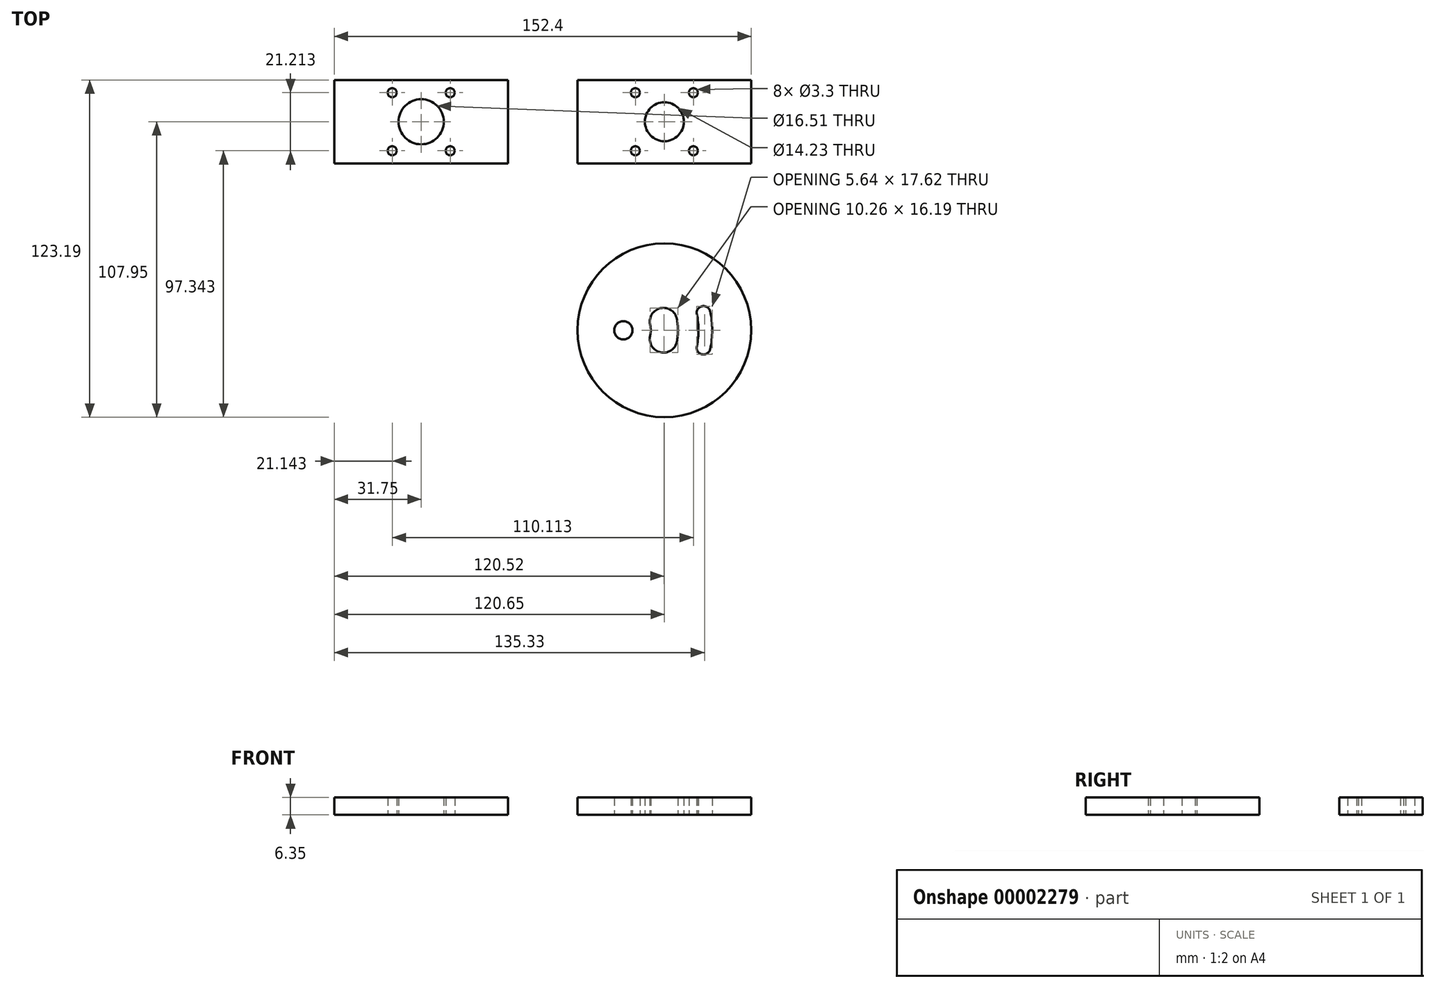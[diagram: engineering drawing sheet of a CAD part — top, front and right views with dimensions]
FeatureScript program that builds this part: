
annotation { "Feature Type Name" : "Feature", "Feature Type Description" : "" }
export const myFeature = defineFeature(function(context is Context, id is Id, definition is map)
    precondition{}
    {
        {
            var Q0;
            Q0=qCreatedBy(makeId("Top.planeOp"),FACE);
            var sketch = newSketch(context, id + "F0", { "sketchPlane" : qUnion([Q0])});
            skCircle(sketch, "E0", {"center": v(0, 0) * mm, "radius": 8.26 * mm});
            skCircle(sketch, "E1", {"center": v(88.9, 0) * mm, "radius": 7.12 * mm});
            skCircle(sketch, "E2", {"center": v(88.9, -76.2) * mm, "radius": 31.75 * mm});
            skCircle(sketch, "E3", {"center": v(73.9, -76.2) * mm, "radius": 3.35 * mm});
            skCircle(sketch, "E4", {"center": v(73.9, -76.2) * mm, "radius": 30 * mm, "construction": true});
            skArc(sketch, "E5", {"start": v(100.78, -82.02) * mm, "mid": v(101.4, -76.2) * mm, "end": v(100.78, -70.38) * mm});
            skArc(sketch, "E6", {"start": v(105.66, -83.08) * mm, "mid": v(106.4, -76.2) * mm, "end": v(105.66, -69.32) * mm});
            skCircle(sketch, "E7", {"center": v(88.9, -76.2) * mm, "radius": 15 * mm, "construction": true});
            skArc(sketch, "E8", {"start": v(103.4, -72.34) * mm, "mid": v(103.52, -72.33) * mm, "end": v(103.65, -72.31) * mm});
            skArc(sketch, "E9", {"start": v(100.78, -82.02) * mm, "mid": v(102.7, -85) * mm, "end": v(105.66, -83.08) * mm});
            skArc(sketch, "E10.trimOffspring", {"start": v(105.66, -69.32) * mm, "mid": v(102.7, -67.4) * mm, "end": v(100.78, -70.38) * mm});
            skArc(sketch, "E11.trimOffspring", {"start": v(103.65, -80.09) * mm, "mid": v(103.52, -80.07) * mm, "end": v(103.4, -80.06) * mm});
            skCircle(sketch, "E12", {"center": v(73.9, -76.2) * mm, "radius": 15 * mm, "construction": true});
            skArc(sketch, "E13", {"start": v(93.45, -71.97) * mm, "mid": v(87.5, -68.14) * mm, "end": v(83.67, -74.08) * mm});
            skArc(sketch, "E14", {"start": v(83.67, -78.32) * mm, "mid": v(87.5, -84.26) * mm, "end": v(93.45, -80.43) * mm});
            skArc(sketch, "E15.trimOffspring", {"start": v(83.67, -78.32) * mm, "mid": v(83.9, -76.2) * mm, "end": v(83.67, -74.08) * mm});
            skArc(sketch, "E16.trimOffspring", {"start": v(93.45, -80.43) * mm, "mid": v(93.9, -76.2) * mm, "end": v(93.45, -71.97) * mm});
            skLineSegment(sketch, "E17", {"start": v(-31.75, 15.24) * mm, "end": v(31.75, 15.24) * mm});
            skLineSegment(sketch, "E18.trimOffspring", {"start": v(57.15, 15.24) * mm, "end": v(120.65, 15.24) * mm});
            skLineSegment(sketch, "E19", {"start": v(0, 0) * mm, "end": v(88.9, 0) * mm, "construction": true});
            skLineSegment(sketch, "E20.0.MirrorCS", {"start": v(-31.75, -15.24) * mm, "end": v(31.75, -15.24) * mm});
            skLineSegment(sketch, "E21.0.MirrorCS", {"start": v(57.15, -15.24) * mm, "end": v(120.65, -15.24) * mm});
            skCircle(sketch, "E22", {"center": v(88.9, 0) * mm, "radius": 15 * mm, "construction": true});
            skLineSegment(sketch, "E23", {"start": v(88.9, 0) * mm, "end": v(88.9, 11.57) * mm, "construction": true});
            skLineSegment(sketch, "E24", {"start": v(88.9, 0) * mm, "end": v(76.23, 12.67) * mm, "construction": true});
            skCircle(sketch, "E25", {"center": v(78.3, 10.6) * mm, "radius": 1.65 * mm});
            skCircle(sketch, "E26.0.MirrorC", {"center": v(99.5, 10.6) * mm, "radius": 1.65 * mm});
            skCircle(sketch, "E27.0.MirrorC", {"center": v(78.3, -10.6) * mm, "radius": 1.65 * mm});
            skCircle(sketch, "E28.0.MirrorC", {"center": v(99.5, -10.6) * mm, "radius": 1.65 * mm});
            skLineSegment(sketch, "E29", {"start": v(31.75, -15.24) * mm, "end": v(31.75, 15.24) * mm});
            skLineSegment(sketch, "E30", {"start": v(-31.75, -15.24) * mm, "end": v(-31.75, 15.24) * mm});
            skLineSegment(sketch, "E31", {"start": v(57.15, 15.24) * mm, "end": v(57.15, -15.24) * mm});
            skLineSegment(sketch, "E32", {"start": v(120.65, -15.24) * mm, "end": v(120.65, 15.24) * mm});
            skPoint(sketch, "E33.center.orphan", {"position": v(15, 0) * mm});
            skPoint(sketch, "E34.center.orphan", {"position": v(0, -15) * mm});
            skPoint(sketch, "E35.center.orphan", {"position": v(-15, 0) * mm});
            skPoint(sketch, "E36.center.orphan", {"position": v(0, 15) * mm});
            skCircle(sketch, "E37", {"center": v(0, 0) * mm, "radius": 15 * mm, "construction": true});
            skCircle(sketch, "E38", {"center": v(-10.6, 10.6) * mm, "radius": 1.65 * mm});
            skLineSegment(sketch, "E39", {"start": v(0, 0) * mm, "end": v(-15.24, 15.24) * mm, "construction": true});
            skCircle(sketch, "E40.0.MirrorC", {"center": v(-10.6, -10.6) * mm, "radius": 1.65 * mm});
            skLineSegment(sketch, "E41", {"start": v(0, 0) * mm, "end": v(0, 10.83) * mm, "construction": true});
            skCircle(sketch, "E42.0.MirrorC", {"center": v(10.6, 10.6) * mm, "radius": 1.65 * mm});
            skCircle(sketch, "E43.0.MirrorC", {"center": v(10.6, -10.6) * mm, "radius": 1.65 * mm});
            skSolve(sketch);
        }
        {
            var Q0;
            Q0 = qSketchRegion(id + "F0", true);
            extrude(context, id + "F1", {"entities" : qUnion([Q0]), "depth" : 6.35 * mm});
        }
    });
